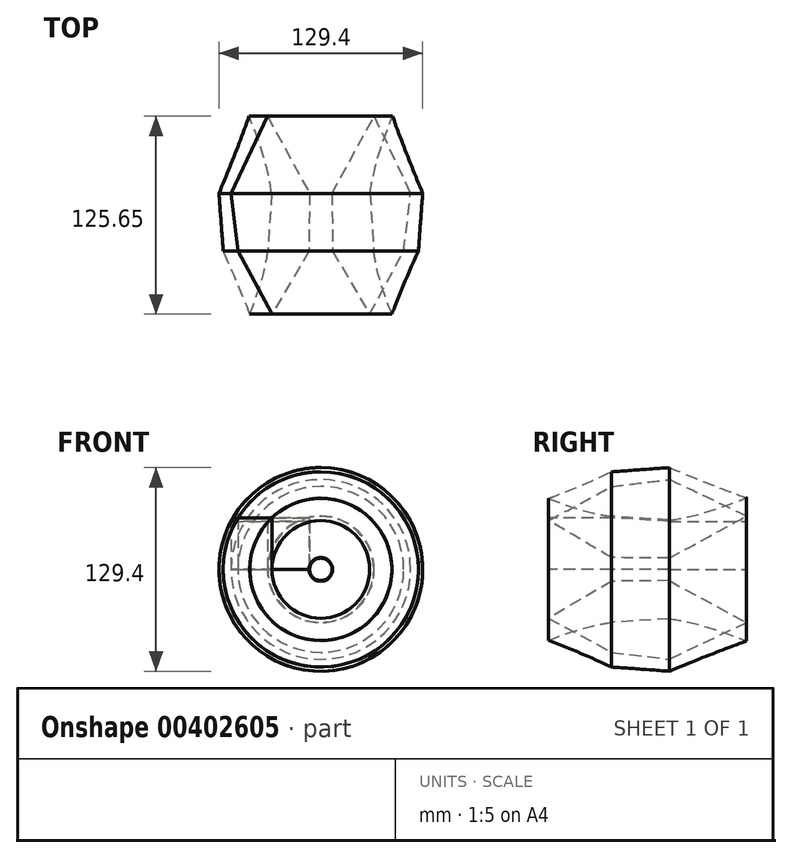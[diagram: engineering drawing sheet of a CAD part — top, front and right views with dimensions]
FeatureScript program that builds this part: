
annotation { "Feature Type Name" : "Feature", "Feature Type Description" : "" }
export const myFeature = defineFeature(function(context is Context, id is Id, definition is map)
    precondition{}
    {
        {
            var Q0;
            Q0=qCreatedBy(makeId("Top.planeOp"),FACE);
            var sketch = newSketch(context, id + "F0", { "sketchPlane" : qUnion([Q0])});
            skLineSegment(sketch, "E0", {"start": v(-57.07, 0) * mm, "end": v(-33.88, 49.04) * mm});
            skLineSegment(sketch, "E1", {"start": v(-33.88, 49.04) * mm, "end": v(-7.13, 0) * mm});
            skLineSegment(sketch, "E2", {"start": v(-7.13, 0) * mm, "end": v(-57.07, 0) * mm});
            skSolve(sketch);
        }
        {
            var Q0;
            Q0=makeQuery(id+"F0.imprint","IMPRINT",FACE,{"disambiguationData":[TD([[makeQuery(id+"F0.imprint","IMPRINT",EDGE,{"derivedFrom":sQuery(id+"F0.wireOp",EDGE,"E0")}),-1.0]])]});
            extrude(context, id + "F1", {"entities" : qUnion([Q0]), "depth" : 30.48 * mm});
        }
        {
            var Q0;
            Q0=qCreatedBy(makeId("Top.planeOp"),FACE);
            var sketch = newSketch(context, id + "F2", { "sketchPlane" : qUnion([Q0])});
            skLineSegment(sketch, "E3", {"start": v(-52.64, -36.66) * mm, "end": v(-7.52, -36.66) * mm});
            skLineSegment(sketch, "E4", {"start": v(-7.52, -36.66) * mm, "end": v(-31.02, -76.6) * mm});
            skLineSegment(sketch, "E5", {"start": v(-52.64, -36.66) * mm, "end": v(-31.02, -76.6) * mm});
            skSolve(sketch);
        }
        {
            var Q0;
            Q0=makeQuery(id+"F2.imprint","IMPRINT",FACE,{"disambiguationData":[TD([[makeQuery(id+"F2.imprint","IMPRINT",EDGE,{"derivedFrom":sQuery(id+"F2.wireOp",EDGE,"E3")}),-1.0]])]});
            extrude(context, id + "F3", {"entities" : qUnion([Q0]), "depth" : 32.77 * mm});
        }
        {
            var Q0;
            Q0=makeQuery(id+"F1.opExtrude","SWEPT_FACE",FACE,{"disambiguationData":[OSD([sQuery(id+"F0.wireOp",EDGE,"E2")])]});
            var Q1;
            Q1=makeQuery(id+"F3.opExtrude","SWEPT_FACE",FACE,{"disambiguationData":[OSD([sQuery(id+"F2.wireOp",EDGE,"E3")])]});
            loft(context, id + "F4", {"sheetProfilesArray" : [{ "sheetProfileEntities" : qUnion([Q0]) }, { "sheetProfileEntities" : qUnion([Q1]) }]});
        }
        {
            var Q0;
            Q0=qCreatedBy(makeId("Top.planeOp"),FACE);
            var sketch = newSketch(context, id + "F5", { "sketchPlane" : qUnion([Q0])});
            skLineSegment(sketch, "E6", {"start": v(0, 54.08) * mm, "end": v(0, -70.07) * mm});
            skSolve(sketch);
        }
        {
            var Q0;
            {var subQ0=sQuery(id+"F2.wireOp",EDGE,"E3");var subQ1=sQuery(id+"F2.wireOp",EDGE,"E4");var subQ2=sQuery(id+"F2.wireOp",EDGE,"E5");var subQ3=sQuery(id+"F0.wireOp",EDGE,"E2");var subQ4=sQuery(id+"F0.wireOp",EDGE,"E1");var subQ5=sQuery(id+"F0.wireOp",EDGE,"E0");Q0=makeQuery(id+"F4.opLoft","SWEPT_FACE",FACE,{"disambiguationData":[OSD([subQ5,subQ4,subQ3,subQ0,subQ1,subQ2]),TDD([makeQuery(id+"F1.opExtrude","CAP_VERTEX",VERTEX,{"disambiguationData":[OSD([subQ5,subQ3])],"isStart":false}),makeQuery(id+"F1.opExtrude","CAP_VERTEX",VERTEX,{"disambiguationData":[OSD([subQ4,subQ3])],"isStart":false}),makeQuery(id+"F1.opExtrude","CAP_EDGE",EDGE,{"disambiguationData":[OSD([subQ3])],"isStart":false}),makeQuery(id+"F3.opExtrude","CAP_VERTEX",VERTEX,{"disambiguationData":[OSD([subQ0,subQ2])],"isStart":false}),makeQuery(id+"F3.opExtrude","CAP_VERTEX",VERTEX,{"disambiguationData":[OSD([subQ0,subQ1])],"isStart":false}),makeQuery(id+"F3.opExtrude","CAP_EDGE",EDGE,{"disambiguationData":[OSD([subQ0])],"isStart":false})])]});}
            var Q1;
            Q1=makeQuery(id+"F1.opExtrude","CAP_FACE",FACE,{"disambiguationData":[OSD([sQuery(id+"F0.wireOp",EDGE,"E0"),sQuery(id+"F0.wireOp",EDGE,"E1"),sQuery(id+"F0.wireOp",EDGE,"E2")])],"isStart":false});
            var Q2;
            Q2=makeQuery(id+"F1.opExtrude","SWEPT_FACE",FACE,{"disambiguationData":[OSD([sQuery(id+"F0.wireOp",EDGE,"E1")])]});
            var Q3;
            Q3=makeQuery(id+"F4.opLoft","SWEPT_FACE",FACE,{"disambiguationData":[OSD([sQuery(id+"F0.wireOp",EDGE,"E1"),sQuery(id+"F0.wireOp",EDGE,"E2"),sQuery(id+"F2.wireOp",EDGE,"E3"),sQuery(id+"F2.wireOp",EDGE,"E4")])]});
            var Q4;
            Q4=makeQuery(id+"F3.opExtrude","SWEPT_FACE",FACE,{"disambiguationData":[OSD([sQuery(id+"F2.wireOp",EDGE,"E4")])]});
            var Q5;
            Q5=makeQuery(id+"F3.opExtrude","CAP_FACE",FACE,{"disambiguationData":[OSD([sQuery(id+"F2.wireOp",EDGE,"E3"),sQuery(id+"F2.wireOp",EDGE,"E4"),sQuery(id+"F2.wireOp",EDGE,"E5")])],"isStart":false});
            var Q6;
            Q6=makeQuery(id+"F1.opExtrude","SWEPT_FACE",FACE,{"disambiguationData":[OSD([sQuery(id+"F0.wireOp",EDGE,"E0")])]});
            var Q7;
            Q7=makeQuery(id+"F4.opLoft","SWEPT_FACE",FACE,{"disambiguationData":[OSD([sQuery(id+"F0.wireOp",EDGE,"E0"),sQuery(id+"F0.wireOp",EDGE,"E2"),sQuery(id+"F2.wireOp",EDGE,"E3"),sQuery(id+"F2.wireOp",EDGE,"E5")])]});
            var Q8;
            {var subQ0=sQuery(id+"F2.wireOp",EDGE,"E3");var subQ1=sQuery(id+"F2.wireOp",EDGE,"E4");var subQ2=sQuery(id+"F2.wireOp",EDGE,"E5");var subQ3=sQuery(id+"F0.wireOp",EDGE,"E2");var subQ4=sQuery(id+"F0.wireOp",EDGE,"E1");var subQ5=sQuery(id+"F0.wireOp",EDGE,"E0");Q8=makeQuery(id+"F4.opLoft","SWEPT_FACE",FACE,{"disambiguationData":[OSD([subQ5,subQ4,subQ3,subQ0,subQ1,subQ2]),TDD([makeQuery(id+"F1.opExtrude","CAP_VERTEX",VERTEX,{"disambiguationData":[OSD([subQ5,subQ3])],"isStart":true}),makeQuery(id+"F1.opExtrude","CAP_VERTEX",VERTEX,{"disambiguationData":[OSD([subQ4,subQ3])],"isStart":true}),makeQuery(id+"F1.opExtrude","CAP_EDGE",EDGE,{"disambiguationData":[OSD([subQ3])],"isStart":true}),makeQuery(id+"F3.opExtrude","CAP_VERTEX",VERTEX,{"disambiguationData":[OSD([subQ0,subQ2])],"isStart":true}),makeQuery(id+"F3.opExtrude","CAP_VERTEX",VERTEX,{"disambiguationData":[OSD([subQ0,subQ1])],"isStart":true}),makeQuery(id+"F3.opExtrude","CAP_EDGE",EDGE,{"disambiguationData":[OSD([subQ0])],"isStart":true})])]});}
            var Q9;
            Q9=makeQuery(id+"F3.opExtrude","CAP_FACE",FACE,{"disambiguationData":[OSD([sQuery(id+"F2.wireOp",EDGE,"E3"),sQuery(id+"F2.wireOp",EDGE,"E4"),sQuery(id+"F2.wireOp",EDGE,"E5")])],"isStart":true});
            var Q10;
            Q10=makeQuery(id+"F3.opExtrude","SWEPT_FACE",FACE,{"disambiguationData":[OSD([sQuery(id+"F2.wireOp",EDGE,"E5")])]});
            var Q11;
            Q11=sQuery(id+"F5.wireOp",EDGE,"E6");
            revolve(context, id + "F6", {"entities" : qUnion([Q0, Q1, Q2, Q3, Q4, Q5, Q6, Q7, Q8, Q9, Q10]), "axis" : qUnion([Q11]), "revolveType" : RevolveType.FULL});
        }
    });
